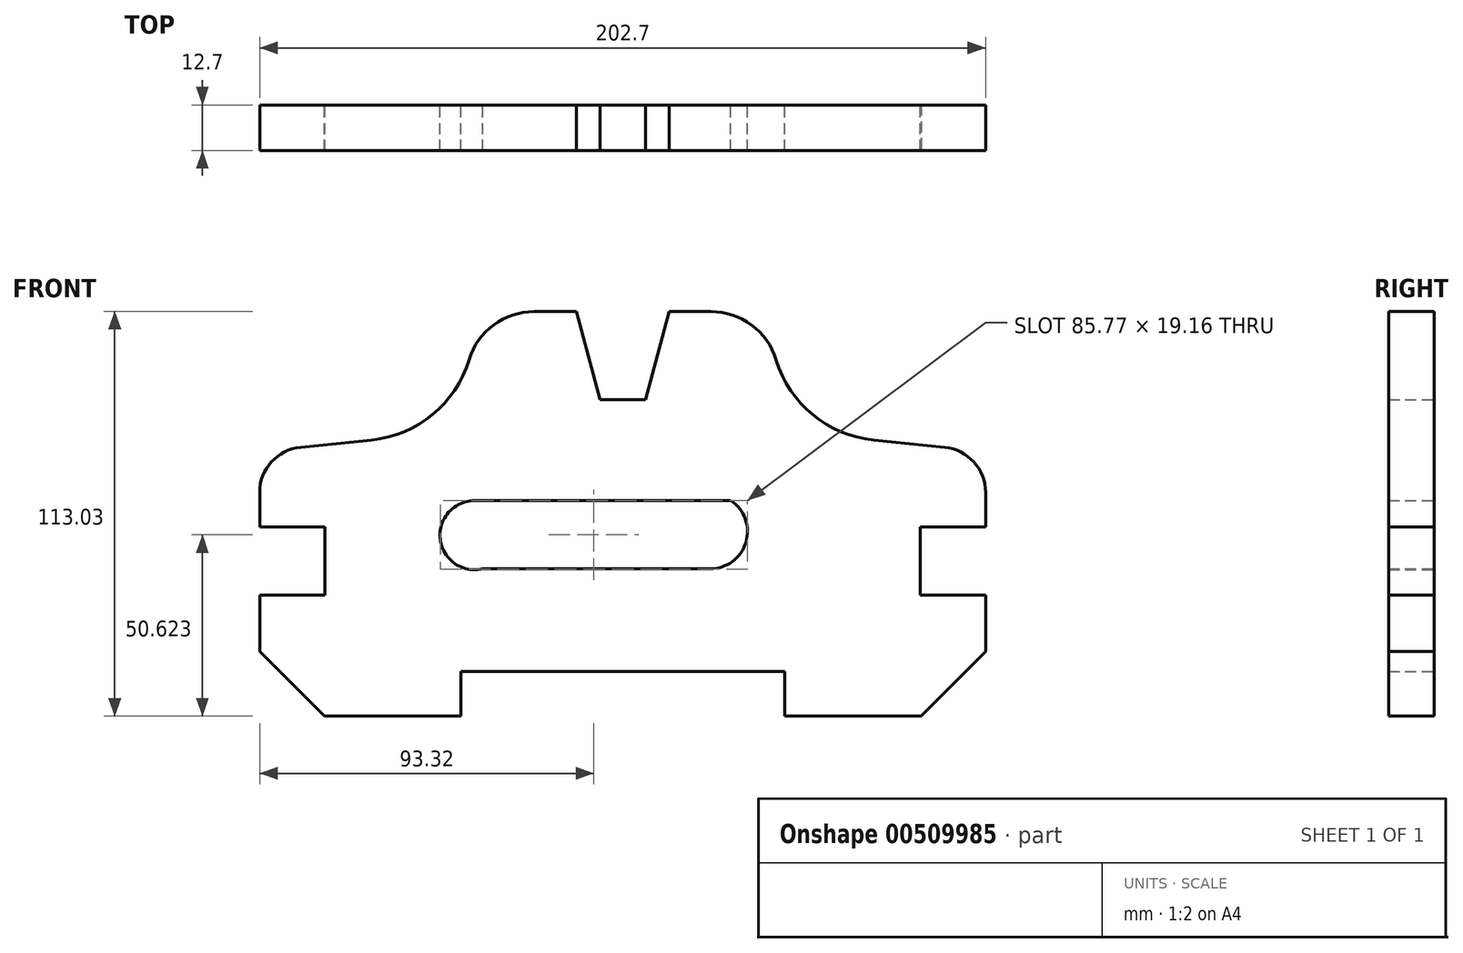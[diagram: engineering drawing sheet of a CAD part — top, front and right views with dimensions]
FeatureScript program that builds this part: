
annotation { "Feature Type Name" : "Feature", "Feature Type Description" : "" }
export const myFeature = defineFeature(function(context is Context, id is Id, definition is map)
    precondition{}
    {
        {
            var Q0;
            Q0=qCreatedBy(makeId("Front.planeOp"),FACE);
            var sketch = newSketch(context, id + "F0", { "sketchPlane" : qUnion([Q0])});
            skLineSegment(sketch, "E0", {"start": v(45.21, -50.04) * mm, "end": v(45.21, -62.48) * mm});
            skLineSegment(sketch, "E1", {"start": v(45.21, -62.48) * mm, "end": v(101.35, -62.48) * mm});
            skLineSegment(sketch, "E2", {"start": v(101.35, -62.48) * mm, "end": v(101.35, -28.7) * mm});
            skLineSegment(sketch, "E3", {"start": v(101.35, -28.7) * mm, "end": v(83.07, -28.7) * mm});
            skLineSegment(sketch, "E4", {"start": v(83.07, -28.7) * mm, "end": v(83.07, -9.65) * mm});
            skLineSegment(sketch, "E5", {"start": v(83.07, -9.65) * mm, "end": v(101.35, -9.65) * mm});
            skLineSegment(sketch, "E6", {"start": v(101.35, -9.65) * mm, "end": v(101.35, 0) * mm});
            skArc(sketch, "E7", {"start": v(101.35, 0) * mm, "mid": v(98.06, 8.52) * mm, "end": v(89.92, 12.64) * mm});
            skLineSegment(sketch, "E8", {"start": v(-45.21, -50.04) * mm, "end": v(45.21, -50.04) * mm});
            skLineSegment(sketch, "E9", {"start": v(0, 61.48) * mm, "end": v(0, -69.08) * mm, "construction": true});
            skLineSegment(sketch, "E10", {"start": v(89.92, 12.64) * mm, "end": v(70.1, 14.63) * mm});
            skArc(sketch, "E11", {"start": v(70.1, 14.63) * mm, "mid": v(53.1, 21.7) * mm, "end": v(42.9, 37.02) * mm});
            skArc(sketch, "E12", {"start": v(42.9, 37.02) * mm, "mid": v(36.01, 46.8) * mm, "end": v(24.66, 50.55) * mm});
            skLineSegment(sketch, "E13", {"start": v(24.66, 50.55) * mm, "end": v(12.95, 50.55) * mm});
            skLineSegment(sketch, "E14", {"start": v(12.95, 50.55) * mm, "end": v(6.35, 25.9) * mm});
            skLineSegment(sketch, "E15.MirrorCS", {"start": v(-12.95, 50.55) * mm, "end": v(-6.35, 25.9) * mm});
            skLineSegment(sketch, "E16.MirrorCS", {"start": v(-24.66, 50.55) * mm, "end": v(-12.95, 50.55) * mm});
            skArc(sketch, "E17.MirrorCS", {"start": v(-42.9, 37.02) * mm, "mid": v(-36.01, 46.8) * mm, "end": v(-24.66, 50.55) * mm});
            skArc(sketch, "E18.MirrorCS", {"start": v(-70.1, 14.63) * mm, "mid": v(-53.1, 21.7) * mm, "end": v(-42.9, 37.02) * mm});
            skLineSegment(sketch, "E19.MirrorCS", {"start": v(-89.92, 12.64) * mm, "end": v(-70.1, 14.63) * mm});
            skArc(sketch, "E20.MirrorCS", {"start": v(-101.35, 0) * mm, "mid": v(-98.06, 8.52) * mm, "end": v(-89.92, 12.64) * mm});
            skLineSegment(sketch, "E21.MirrorCS", {"start": v(-101.35, -9.65) * mm, "end": v(-101.35, 0) * mm});
            skLineSegment(sketch, "E22.MirrorCS", {"start": v(-83.07, -9.65) * mm, "end": v(-101.35, -9.65) * mm});
            skLineSegment(sketch, "E23.MirrorCS", {"start": v(-83.07, -28.7) * mm, "end": v(-83.07, -9.65) * mm});
            skLineSegment(sketch, "E24.MirrorCS", {"start": v(-101.35, -28.7) * mm, "end": v(-83.07, -28.7) * mm});
            skLineSegment(sketch, "E25.MirrorCS", {"start": v(-101.35, -62.48) * mm, "end": v(-101.35, -28.7) * mm});
            skLineSegment(sketch, "E26.MirrorCS", {"start": v(-45.21, -62.48) * mm, "end": v(-101.35, -62.48) * mm});
            skLineSegment(sketch, "E27.MirrorCS", {"start": v(-45.21, -50.04) * mm, "end": v(-45.21, -62.48) * mm});
            skLineSegment(sketch, "E28", {"start": v(-6.35, 25.9) * mm, "end": v(6.35, 25.9) * mm});
            skLineSegment(sketch, "E29", {"start": v(-6.35, 25.9) * mm, "end": v(-6.35, 72.38) * mm, "construction": true});
            skLineSegment(sketch, "E30", {"start": v(-41.32, -2.28) * mm, "end": v(30.21, -2.28) * mm});
            skLineSegment(sketch, "E31", {"start": v(-39.03, -21.33) * mm, "end": v(24.47, -21.33) * mm});
            skArc(sketch, "E32", {"start": v(24.47, -21.33) * mm, "mid": v(34.42, -13.93) * mm, "end": v(30.21, -2.28) * mm});
            skArc(sketch, "E33", {"start": v(-41.32, -2.28) * mm, "mid": v(-50.92, -13.1) * mm, "end": v(-39.03, -21.33) * mm});
            skLineSegment(sketch, "E34", {"start": v(24.47, -10.94) * mm, "end": v(24.47, -44.82) * mm, "construction": true});
            skSolve(sketch);
        }
        {
            var Q0;
            Q0 = qSketchRegion(id + "F0", true);
            extrude(context, id + "F1", {"entities" : qUnion([Q0]), "endBound" : BoundingType.SYMMETRIC, "depth" : 12.7 * mm, "offsetDistance" : 25.4 * mm});
        }
        {
            var Q0;
            Q0=makeQuery(id+"F1.opExtrude","SWEPT_EDGE",EDGE,{"disambiguationData":[OSD([sQuery(id+"F0.wireOp",EDGE,"E25.MirrorCS"),sQuery(id+"F0.wireOp",EDGE,"E26.MirrorCS")])]});
            var Q1;
            Q1=makeQuery(id+"F1.opExtrude","SWEPT_EDGE",EDGE,{"disambiguationData":[OSD([sQuery(id+"F0.wireOp",EDGE,"E1"),sQuery(id+"F0.wireOp",EDGE,"E2")])]});
            chamfer(context, id + "F2", {"entities" : qUnion([Q0, Q1]), "width" : 18.03 * mm, "tangentPropagation" : true});
        }
    });
